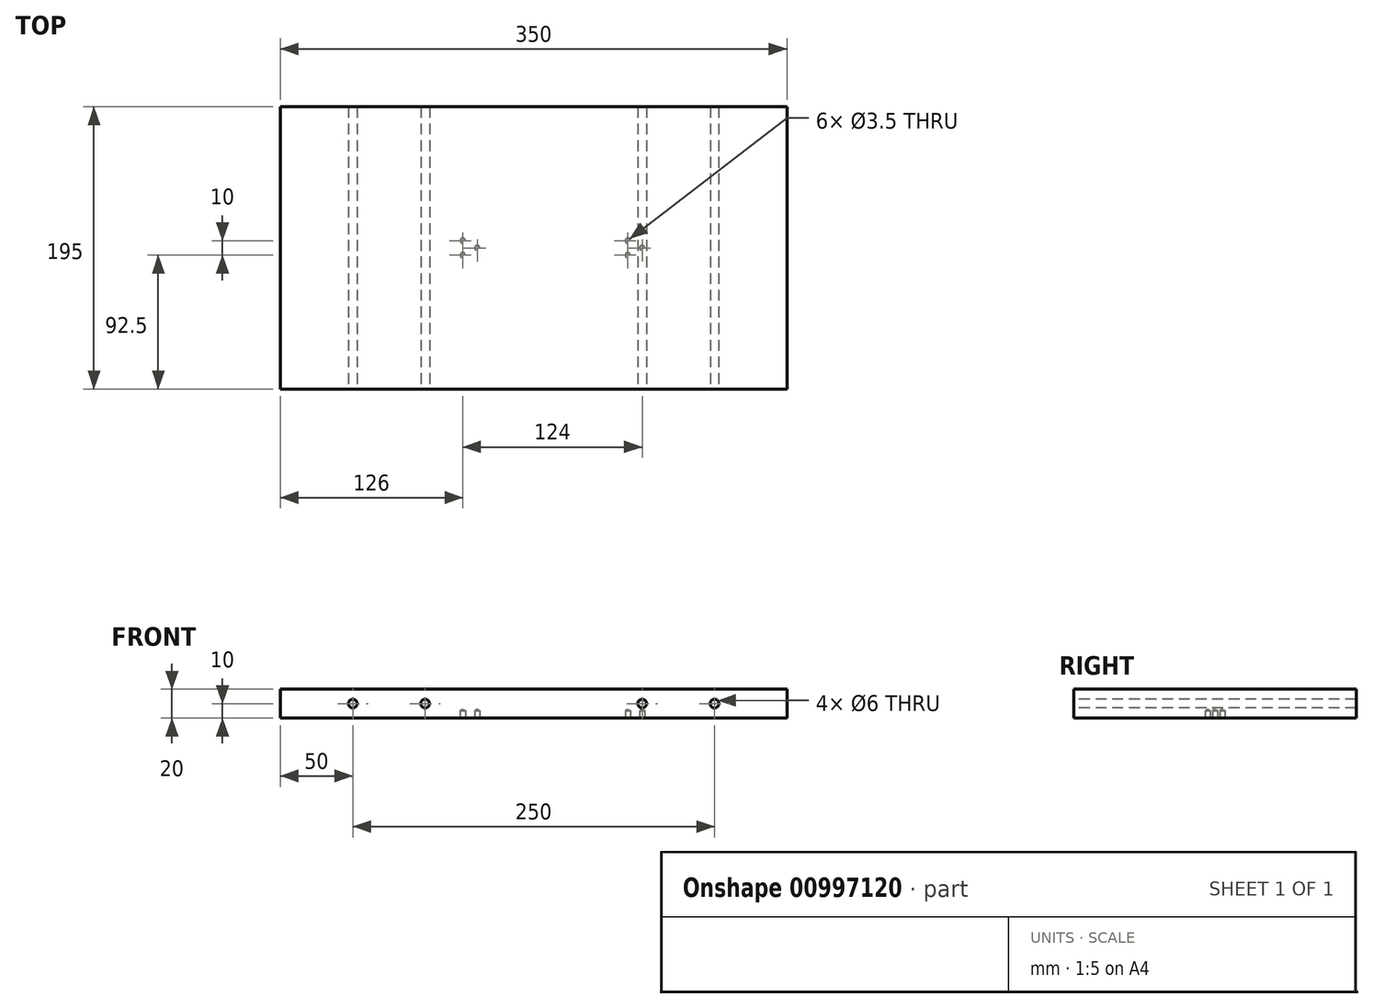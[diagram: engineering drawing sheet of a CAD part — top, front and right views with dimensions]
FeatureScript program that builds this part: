
annotation { "Feature Type Name" : "Feature", "Feature Type Description" : "" }
export const myFeature = defineFeature(function(context is Context, id is Id, definition is map)
    precondition{}
    {
        {
            var Q0;
            Q0=qCreatedBy(makeId("Top.planeOp"),FACE);
            var sketch = newSketch(context, id + "F0", { "sketchPlane" : qUnion([Q0])});
            skLineSegment(sketch, "E0.bottom", {"start": v(175, 97.5) * mm, "end": v(-175, 97.5) * mm});
            skLineSegment(sketch, "E0.top", {"start": v(175, -97.5) * mm, "end": v(-175, -97.5) * mm});
            skLineSegment(sketch, "E0.left", {"start": v(175, 97.5) * mm, "end": v(175, -97.5) * mm});
            skLineSegment(sketch, "E0.right", {"start": v(-175, 97.5) * mm, "end": v(-175, -97.5) * mm});
            skPoint(sketch, "E0.middle", {"position": v(0, 0) * mm});
            skSolve(sketch);
        }
        {
            var Q0;
            Q0 = qSketchRegion(id + "F0", true);
            extrude(context, id + "F1", {"entities" : qUnion([Q0]), "endBound" : BoundingType.SYMMETRIC, "depth" : 20 * mm, "offsetDistance" : 25 * mm});
        }
        {
            var Q0;
            Q0=makeQuery(id+"F1.opExtrude","SWEPT_FACE",FACE,{"disambiguationData":[OSD([sQuery(id+"F0.wireOp",EDGE,"E0.top")])]});
            var sketch = newSketch(context, id + "F2", { "sketchPlane" : qUnion([Q0])});
            skPoint(sketch, "E1", {"position": v(-125, 0) * mm});
            skPoint(sketch, "E2", {"position": v(-75, 0) * mm});
            skPoint(sketch, "E3", {"position": v(75, 0) * mm});
            skPoint(sketch, "E4", {"position": v(125, 0) * mm});
            skSolve(sketch);
        }
        {
            var Q0;
            Q0=sQuery(id+"F2.wireOp",VERTEX,"E1");
            var Q1;
            Q1=sQuery(id+"F2.wireOp",VERTEX,"E2");
            var Q2;
            Q2=sQuery(id+"F2.wireOp",VERTEX,"E3");
            var Q3;
            Q3=sQuery(id+"F2.wireOp",VERTEX,"E4");
            var Q4;
            Q4=makeQuery(id+"F1.opExtrude","SWEPT_BODY",BODY,{"disambiguationData":[OSD([sQuery(id+"F0.wireOp",EDGE,"E0.bottom"),sQuery(id+"F0.wireOp",EDGE,"E0.top"),sQuery(id+"F0.wireOp",EDGE,"E0.left"),sQuery(id+"F0.wireOp",EDGE,"E0.right")])]});
            hole(context, id + "F3", {"style" : HoleStyle.SIMPLE, "endStyle" : HoleEndStyle.THROUGH, "holeDiameter" : 6 * mm, "majorDiameter" : 5 * mm, "isTappedThrough" : true, "tappedDepth" : 12 * mm, "tapClearance" : 3, "locations" : qUnion([Q0, Q1, Q2, Q3]), "scope" : qUnion([Q4])});
        }
        {
            var Q0;
            Q0=makeQuery(id+"F1.opExtrude","CAP_FACE",FACE,{"disambiguationData":[OSD([sQuery(id+"F0.wireOp",EDGE,"E0.bottom"),sQuery(id+"F0.wireOp",EDGE,"E0.top"),sQuery(id+"F0.wireOp",EDGE,"E0.left"),sQuery(id+"F0.wireOp",EDGE,"E0.right")])],"isStart":true});
            var sketch = newSketch(context, id + "F4", { "sketchPlane" : qUnion([Q0])});
            skPoint(sketch, "E5", {"position": v(-49, 5) * mm});
            skPoint(sketch, "E6", {"position": v(-49, -5) * mm});
            skPoint(sketch, "E7", {"position": v(-39, 0) * mm});
            skPoint(sketch, "E8", {"position": v(65, 5) * mm});
            skPoint(sketch, "E9", {"position": v(65, -5) * mm});
            skPoint(sketch, "E10", {"position": v(75, 0) * mm});
            skSolve(sketch);
        }
        {
            var Q0;
            Q0=sQuery(id+"F4.wireOp",VERTEX,"E5");
            var Q1;
            Q1=sQuery(id+"F4.wireOp",VERTEX,"E6");
            var Q2;
            Q2=sQuery(id+"F4.wireOp",VERTEX,"E7");
            var Q3;
            Q3=sQuery(id+"F4.wireOp",VERTEX,"E8");
            var Q4;
            Q4=sQuery(id+"F4.wireOp",VERTEX,"E9");
            var Q5;
            Q5=sQuery(id+"F4.wireOp",VERTEX,"E10");
            var Q6;
            Q6=makeQuery(id+"F1.opExtrude","SWEPT_BODY",BODY,{"disambiguationData":[OSD([sQuery(id+"F0.wireOp",EDGE,"E0.bottom"),sQuery(id+"F0.wireOp",EDGE,"E0.top"),sQuery(id+"F0.wireOp",EDGE,"E0.left"),sQuery(id+"F0.wireOp",EDGE,"E0.right")])]});
            hole(context, id + "F5", {"style" : HoleStyle.SIMPLE, "endStyle" : HoleEndStyle.BLIND, "holeDiameter" : 3.5 * mm, "majorDiameter" : 5 * mm, "holeDepth" : 5 * mm, "isTappedThrough" : true, "tappedDepth" : 12 * mm, "tapClearance" : 3, "locations" : qUnion([Q0, Q1, Q2, Q3, Q4, Q5]), "scope" : qUnion([Q6])});
        }
    });
